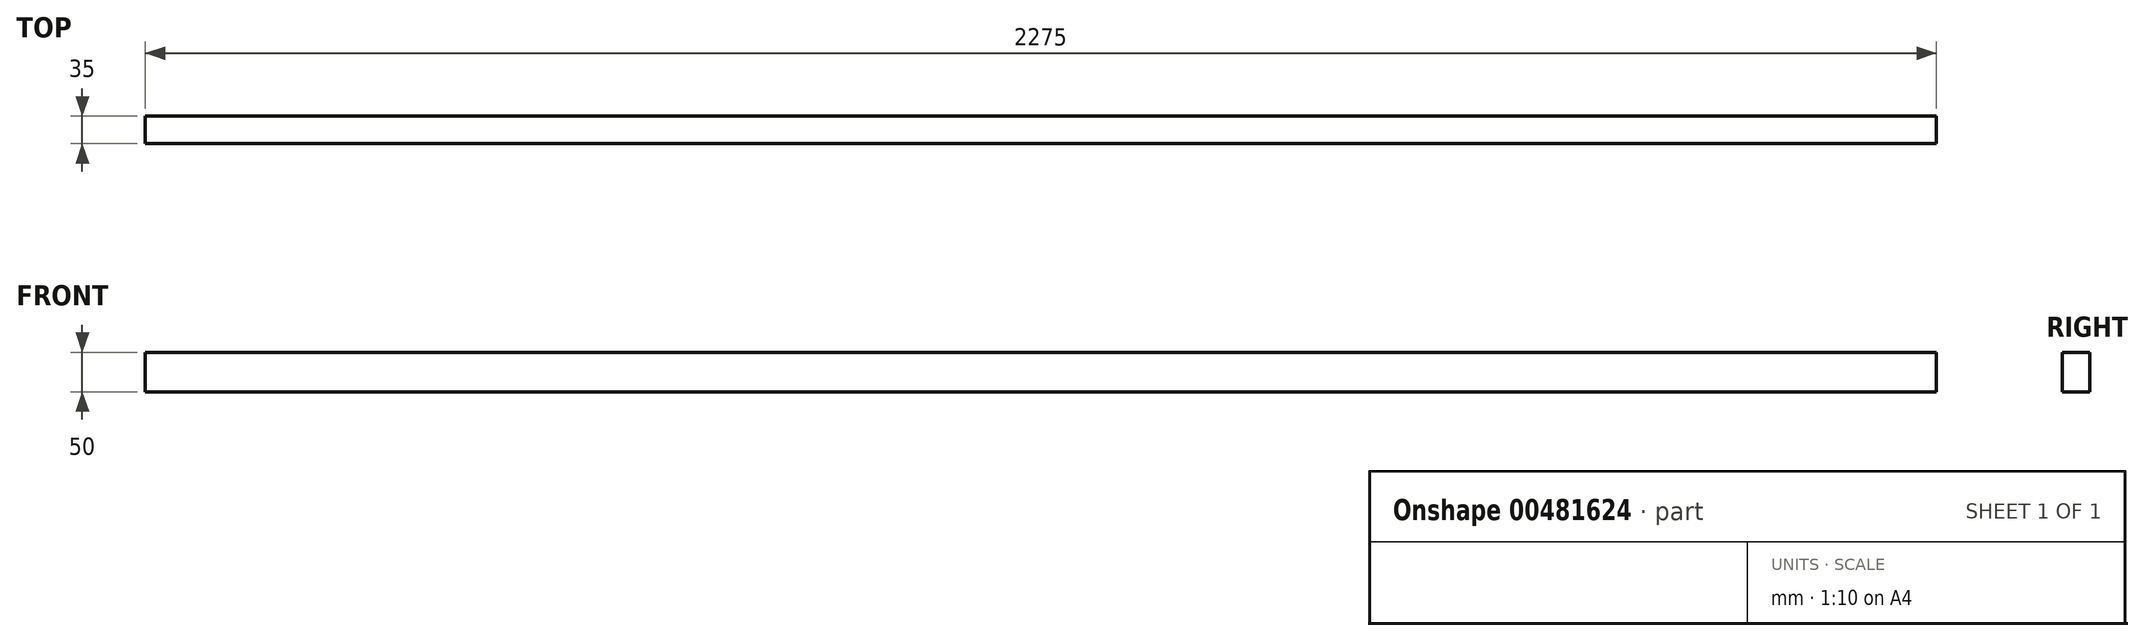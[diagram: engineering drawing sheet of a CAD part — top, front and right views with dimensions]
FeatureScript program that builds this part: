
annotation { "Feature Type Name" : "Feature", "Feature Type Description" : "" }
export const myFeature = defineFeature(function(context is Context, id is Id, definition is map)
    precondition{}
    {
        {
            var Q0;
            Q0=qCreatedBy(makeId("Top.planeOp"),FACE);
            var sketch = newSketch(context, id + "F0", { "sketchPlane" : qUnion([Q0])});
            skLineSegment(sketch, "E0.bottom", {"start": v(-2275, -35) * mm, "end": v(0, -35) * mm});
            skLineSegment(sketch, "E0.top", {"start": v(-2275, 0) * mm, "end": v(0, 0) * mm});
            skLineSegment(sketch, "E0.left", {"start": v(-2275, -35) * mm, "end": v(-2275, 0) * mm});
            skLineSegment(sketch, "E0.right", {"start": v(0, -35) * mm, "end": v(0, 0) * mm});
            skSolve(sketch);
        }
        {
            var Q0;
            Q0 = qSketchRegion(id + "F0", true);
            extrude(context, id + "F1", {"entities" : qUnion([Q0]), "depth" : 50 * mm});
        }
    });
